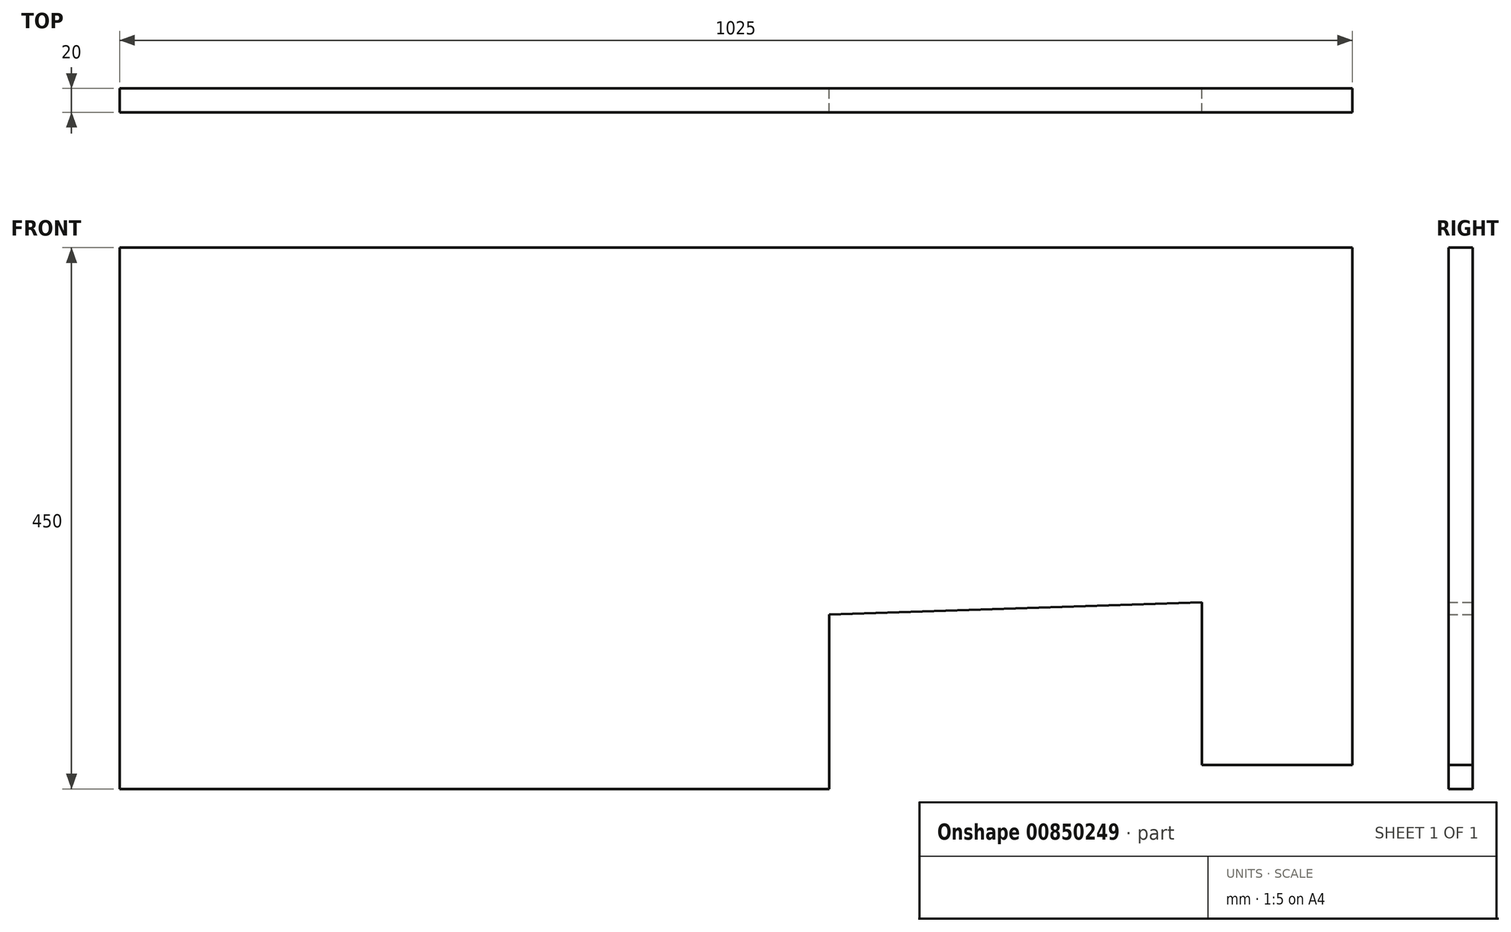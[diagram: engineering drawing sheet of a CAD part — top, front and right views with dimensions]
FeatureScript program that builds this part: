
annotation { "Feature Type Name" : "Feature", "Feature Type Description" : "" }
export const myFeature = defineFeature(function(context is Context, id is Id, definition is map)
    precondition{}
    {
        {
            var Q0;
            Q0=qCreatedBy(makeId("Front.planeOp"),FACE);
            var sketch = newSketch(context, id + "F0", { "sketchPlane" : qUnion([Q0])});
            skPoint(sketch, "E0.0", {"position": v(0, 0) * mm});
            skLineSegment(sketch, "E1", {"start": v(0, 0) * mm, "end": v(0, 0) * mm});
            skLineSegment(sketch, "E2", {"start": v(512.72, 0) * mm, "end": v(-512.28, 0) * mm});
            skLineSegment(sketch, "E3", {"start": v(-512.28, 0) * mm, "end": v(-512.28, -450) * mm});
            skLineSegment(sketch, "E4", {"start": v(-512.28, -450) * mm, "end": v(77.72, -450) * mm});
            skPoint(sketch, "E5.start.orphan", {"position": v(521.57, 0) * mm});
            skLineSegment(sketch, "E6", {"start": v(512.72, 0) * mm, "end": v(512.72, -430) * mm});
            skLineSegment(sketch, "E7", {"start": v(512.72, -430) * mm, "end": v(387.72, -430) * mm});
            skLineSegment(sketch, "E8", {"start": v(387.72, -169.39) * mm, "end": v(387.72, -169.39) * mm});
            skLineSegment(sketch, "E9", {"start": v(387.72, -430) * mm, "end": v(387.72, -295) * mm});
            skPoint(sketch, "E10.end.orphan", {"position": v(77.72, -295) * mm});
            skLineSegment(sketch, "E11", {"start": v(77.72, -450) * mm, "end": v(77.72, -305) * mm});
            skLineSegment(sketch, "E12", {"start": v(387.72, -295) * mm, "end": v(77.72, -305) * mm});
            skSolve(sketch);
        }
        {
            var Q0;
            Q0=makeQuery(id+"F0.imprint","IMPRINT",FACE,{"disambiguationData":[TD([[makeQuery(id+"F0.imprint","IMPRINT",EDGE,{"derivedFrom":sQuery(id+"F0.wireOp",EDGE,"E2")}),1.0]])]});
            extrude(context, id + "F1", {"entities" : qUnion([Q0]), "depth" : 20 * mm, "offsetDistance" : 25 * mm});
        }
    });
